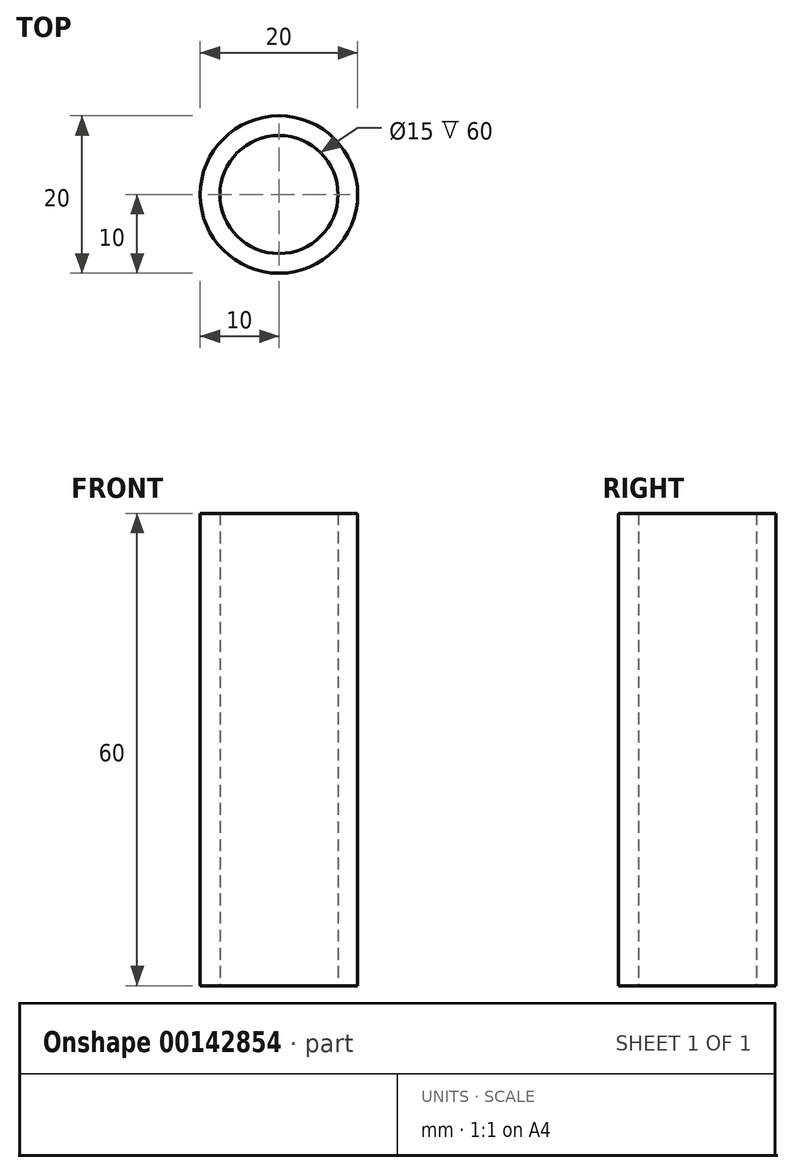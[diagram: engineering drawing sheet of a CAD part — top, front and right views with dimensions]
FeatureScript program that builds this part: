
annotation { "Feature Type Name" : "Feature", "Feature Type Description" : "" }
export const myFeature = defineFeature(function(context is Context, id is Id, definition is map)
    precondition{}
    {
        {
            var Q0;
            Q0=qCreatedBy(makeId("Top.planeOp"),FACE);
            var sketch = newSketch(context, id + "F0", { "sketchPlane" : qUnion([Q0])});
            skCircle(sketch, "E0", {"center": v(0, 0) * mm, "radius": 7.5 * mm});
            skCircle(sketch, "E1", {"center": v(0, 0) * mm, "radius": 10 * mm});
            skSolve(sketch);
        }
        {
            var Q0;
            Q0 = qSketchRegion(id + "F0", true);
            extrude(context, id + "F1", {"entities" : qUnion([Q0]), "depth" : 60 * mm});
        }
    });
